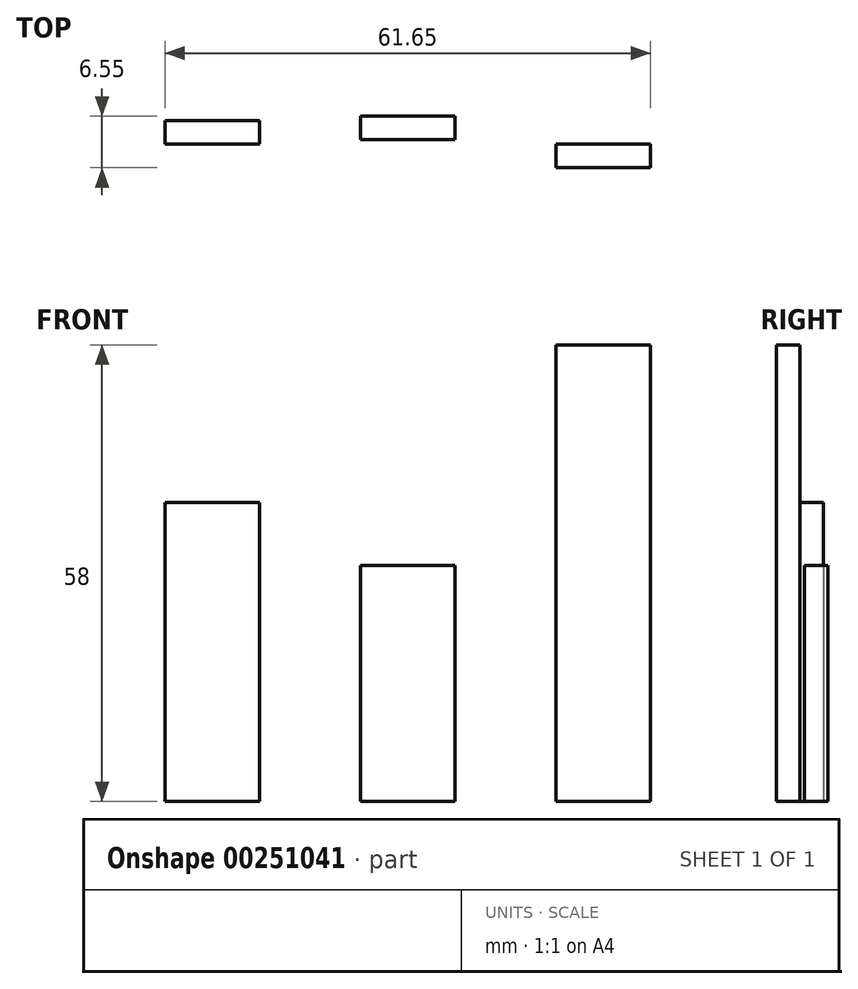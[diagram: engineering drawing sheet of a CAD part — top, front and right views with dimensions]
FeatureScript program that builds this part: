
annotation { "Feature Type Name" : "Feature", "Feature Type Description" : "" }
export const myFeature = defineFeature(function(context is Context, id is Id, definition is map)
    precondition{}
    {
        {
            var Q0;
            Q0=qCreatedBy(makeId("Top.planeOp"),FACE);
            var sketch = newSketch(context, id + "F0", { "sketchPlane" : qUnion([Q0])});
            skLineSegment(sketch, "E0", {"start": v(-27.69, 9.84) * mm, "end": v(-27.69, 12.84) * mm});
            skLineSegment(sketch, "E1", {"start": v(-27.69, 12.84) * mm, "end": v(-15.69, 12.84) * mm});
            skLineSegment(sketch, "E2", {"start": v(-15.69, 12.84) * mm, "end": v(-15.69, 9.84) * mm});
            skLineSegment(sketch, "E3", {"start": v(-15.69, 9.84) * mm, "end": v(-27.69, 9.84) * mm});
            skSolve(sketch);
        }
        {
            var Q0;
            Q0 = qSketchRegion(id + "F0", true);
            extrude(context, id + "F1", {"entities" : qUnion([Q0]), "depth" : 38 * mm});
        }
        {
            var Q0;
            Q0=qCreatedBy(makeId("Top.planeOp"),FACE);
            var sketch = newSketch(context, id + "F2", { "sketchPlane" : qUnion([Q0])});
            skLineSegment(sketch, "E4", {"start": v(-2.86, 10.42) * mm, "end": v(-2.86, 13.42) * mm});
            skLineSegment(sketch, "E5", {"start": v(-2.86, 13.42) * mm, "end": v(9.14, 13.42) * mm});
            skLineSegment(sketch, "E6", {"start": v(9.14, 13.42) * mm, "end": v(9.14, 10.42) * mm});
            skLineSegment(sketch, "E7", {"start": v(9.14, 10.42) * mm, "end": v(-2.86, 10.42) * mm});
            skSolve(sketch);
        }
        {
            var Q0;
            Q0 = qSketchRegion(id + "F2", true);
            extrude(context, id + "F3", {"entities" : qUnion([Q0]), "depth" : 30 * mm});
        }
        {
            var Q0;
            Q0=qCreatedBy(makeId("Top.planeOp"),FACE);
            var sketch = newSketch(context, id + "F4", { "sketchPlane" : qUnion([Q0])});
            skLineSegment(sketch, "E8", {"start": v(21.96, 9.87) * mm, "end": v(21.96, 6.87) * mm});
            skLineSegment(sketch, "E9", {"start": v(21.96, 6.87) * mm, "end": v(33.96, 6.87) * mm});
            skLineSegment(sketch, "E10", {"start": v(33.96, 6.87) * mm, "end": v(33.96, 9.87) * mm});
            skLineSegment(sketch, "E11", {"start": v(33.96, 9.87) * mm, "end": v(21.96, 9.87) * mm});
            skSolve(sketch);
        }
        {
            var Q0;
            Q0 = qSketchRegion(id + "F4", true);
            extrude(context, id + "F5", {"entities" : qUnion([Q0]), "depth" : 58 * mm});
        }
    });
